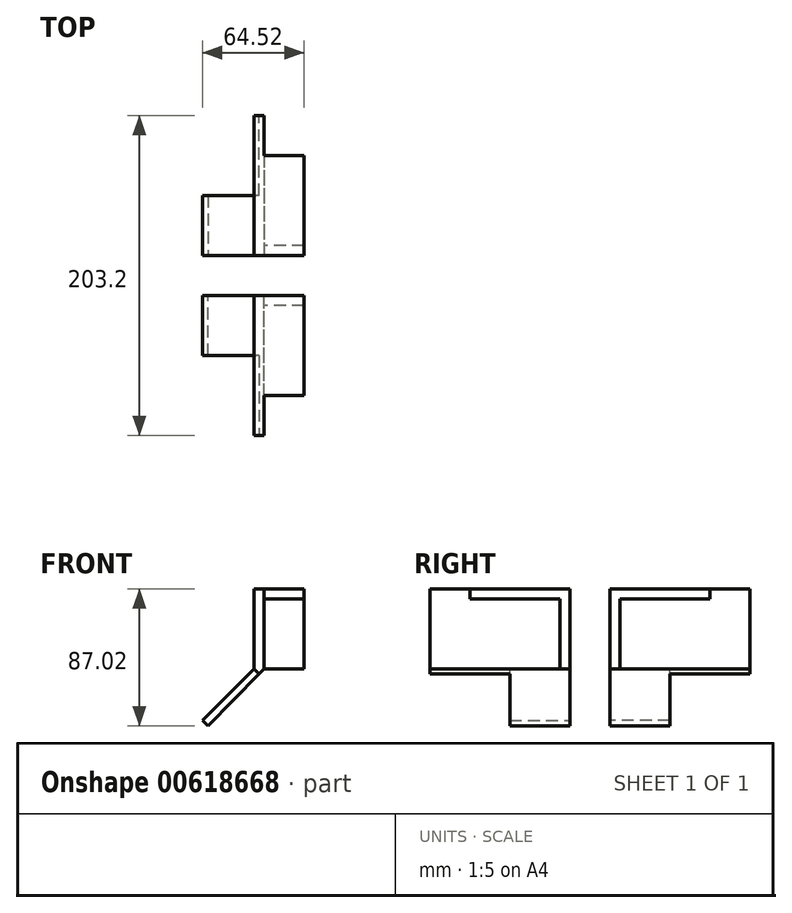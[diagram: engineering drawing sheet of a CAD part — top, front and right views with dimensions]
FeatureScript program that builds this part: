
annotation { "Feature Type Name" : "Feature", "Feature Type Description" : "" }
export const myFeature = defineFeature(function(context is Context, id is Id, definition is map)
    precondition{}
    {
        {
            var Q0;
            Q0=qCreatedBy(makeId("Front.planeOp"),FACE);
            var sketch = newSketch(context, id + "F0", { "sketchPlane" : qUnion([Q0])});
            skLineSegment(sketch, "E0", {"start": v(0, 0) * mm, "end": v(0, 50.8) * mm});
            skLineSegment(sketch, "E1", {"start": v(0, 50.8) * mm, "end": v(6.35, 50.8) * mm});
            skLineSegment(sketch, "E2", {"start": v(6.35, 50.8) * mm, "end": v(6.35, 0) * mm});
            skLineSegment(sketch, "E3", {"start": v(6.35, 0) * mm, "end": v(-29.27, -36.22) * mm});
            skLineSegment(sketch, "E4", {"start": v(-29.27, -36.22) * mm, "end": v(-32.77, -32.77) * mm});
            skLineSegment(sketch, "E5", {"start": v(-32.77, -32.77) * mm, "end": v(0, 0) * mm});
            skSolve(sketch);
        }
        {
            var Q0;
            Q0=makeQuery(id+"F0.imprint","IMPRINT",FACE,{"disambiguationData":[TD([[makeQuery(id+"F0.imprint","IMPRINT",EDGE,{"derivedFrom":sQuery(id+"F0.wireOp",EDGE,"E0")}),-1.0]])]});
            extrude(context, id + "F1", {"entities" : qUnion([Q0]), "depth" : 88.9 * mm, "offsetDistance" : 25.4 * mm});
        }
        {
            var Q0;
            Q0=makeQuery(id+"F1.opExtrude","SWEPT_FACE",FACE,{"disambiguationData":[OSD([sQuery(id+"F0.wireOp",EDGE,"E5")])]});
            var sketch = newSketch(context, id + "F2", { "sketchPlane" : qUnion([Q0])});
            skLineSegment(sketch, "E6.bottom", {"start": v(88.9, 0) * mm, "end": v(38.1, 0) * mm});
            skLineSegment(sketch, "E6.top", {"start": v(88.9, -46.35) * mm, "end": v(38.1, -46.35) * mm});
            skLineSegment(sketch, "E6.left", {"start": v(88.9, 0) * mm, "end": v(88.9, -46.35) * mm});
            skLineSegment(sketch, "E6.right", {"start": v(38.1, 0) * mm, "end": v(38.1, -46.35) * mm});
            skSolve(sketch);
        }
        {
            var Q0;
            Q0=makeQuery(id+"F2.imprint","IMPRINT",FACE,{"disambiguationData":[TD([[makeQuery(id+"F2.imprint","IMPRINT",EDGE,{"derivedFrom":sQuery(id+"F2.wireOp",EDGE,"E6.bottom")}),1.0]])]});
            extrude(context, id + "F3", {"entities" : qUnion([Q0]), "operationType" : NewBodyOperationType.REMOVE, "oppositeDirection" : true, "depth" : 25.4 * mm, "offsetDistance" : 25.4 * mm});
        }
        {
            var Q0;
            Q0=makeQuery(id+"F1.opExtrude","SWEPT_FACE",FACE,{"disambiguationData":[OSD([sQuery(id+"F0.wireOp",EDGE,"E2")])]});
            var sketch = newSketch(context, id + "F4", { "sketchPlane" : qUnion([Q0])});
            skLineSegment(sketch, "E7.bottom", {"start": v(0, 50.8) * mm, "end": v(-6.35, 50.8) * mm});
            skLineSegment(sketch, "E7.top", {"start": v(0, 0) * mm, "end": v(-6.35, 0) * mm});
            skLineSegment(sketch, "E7.left", {"start": v(0, 50.8) * mm, "end": v(0, 0) * mm});
            skLineSegment(sketch, "E7.right", {"start": v(-6.35, 50.8) * mm, "end": v(-6.35, 0) * mm});
            skSolve(sketch);
        }
        {
            var Q0;
            Q0=makeQuery(id+"F4.imprint","IMPRINT",FACE,{"disambiguationData":[TD([[makeQuery(id+"F4.imprint","IMPRINT",EDGE,{"derivedFrom":sQuery(id+"F4.wireOp",EDGE,"E7.bottom")}),-1.0]])]});
            extrude(context, id + "F5", {"entities" : qUnion([Q0]), "operationType" : NewBodyOperationType.ADD, "depth" : 25.4 * mm, "offsetDistance" : 25.4 * mm});
        }
        {
            var Q0;
            Q0=makeQuery(id+"F1.opExtrude","SWEPT_FACE",FACE,{"disambiguationData":[OSD([sQuery(id+"F0.wireOp",EDGE,"E2")])]});
            var sketch = newSketch(context, id + "F6", { "sketchPlane" : qUnion([Q0])});
            skLineSegment(sketch, "E8.bottom", {"start": v(-63.5, 50.8) * mm, "end": v(-6.35, 50.8) * mm});
            skLineSegment(sketch, "E8.top", {"start": v(-63.5, 44.45) * mm, "end": v(-6.35, 44.45) * mm});
            skLineSegment(sketch, "E8.left", {"start": v(-63.5, 50.8) * mm, "end": v(-63.5, 44.45) * mm});
            skLineSegment(sketch, "E8.right", {"start": v(-6.35, 50.8) * mm, "end": v(-6.35, 44.45) * mm});
            skSolve(sketch);
        }
        {
            var Q0;
            Q0=makeQuery(id+"F6.imprint","IMPRINT",FACE,{"disambiguationData":[TD([[makeQuery(id+"F6.imprint","IMPRINT",EDGE,{"derivedFrom":sQuery(id+"F6.wireOp",EDGE,"E8.bottom")}),-1.0]])]});
            extrude(context, id + "F7", {"entities" : qUnion([Q0]), "operationType" : NewBodyOperationType.ADD, "depth" : 25.4 * mm, "offsetDistance" : 25.4 * mm});
        }
        {
            var Q0;
            Q0=makeQuery(id+"F1.opExtrude","SWEPT_BODY",BODY,{"disambiguationData":[OSD([sQuery(id+"F0.wireOp",EDGE,"E0"),sQuery(id+"F0.wireOp",EDGE,"E1"),sQuery(id+"F0.wireOp",EDGE,"E2"),sQuery(id+"F0.wireOp",EDGE,"E3"),sQuery(id+"F0.wireOp",EDGE,"E4"),sQuery(id+"F0.wireOp",EDGE,"E5")])]});
            var Q1;
            Q1=qCreatedBy(makeId("Front.planeOp"),FACE);
            mirror(context, id + "F8", {"entities" : qUnion([Q0]), "mirrorPlane" : qUnion([Q1])});
        }
        {
            var Q0;
            Q0=makeQuery(id+"F8.opPattern","COPY",BODY,{"derivedFrom":makeQuery(id+"F1.opExtrude","SWEPT_BODY",BODY,{"disambiguationData":[OSD([sQuery(id+"F0.wireOp",EDGE,"E0"),sQuery(id+"F0.wireOp",EDGE,"E1"),sQuery(id+"F0.wireOp",EDGE,"E2"),sQuery(id+"F0.wireOp",EDGE,"E3"),sQuery(id+"F0.wireOp",EDGE,"E4"),sQuery(id+"F0.wireOp",EDGE,"E5")])]}),"instanceName":"1"});
            transform(context, id + "F9", {"entities" : qUnion([Q0]), "transformType" : TransformType.TRANSLATION_3D, "dx" : 0 * mm, "dy" : 25.4 * mm, "dz" : 0 * mm, "makeCopy" : false});
        }
    });
